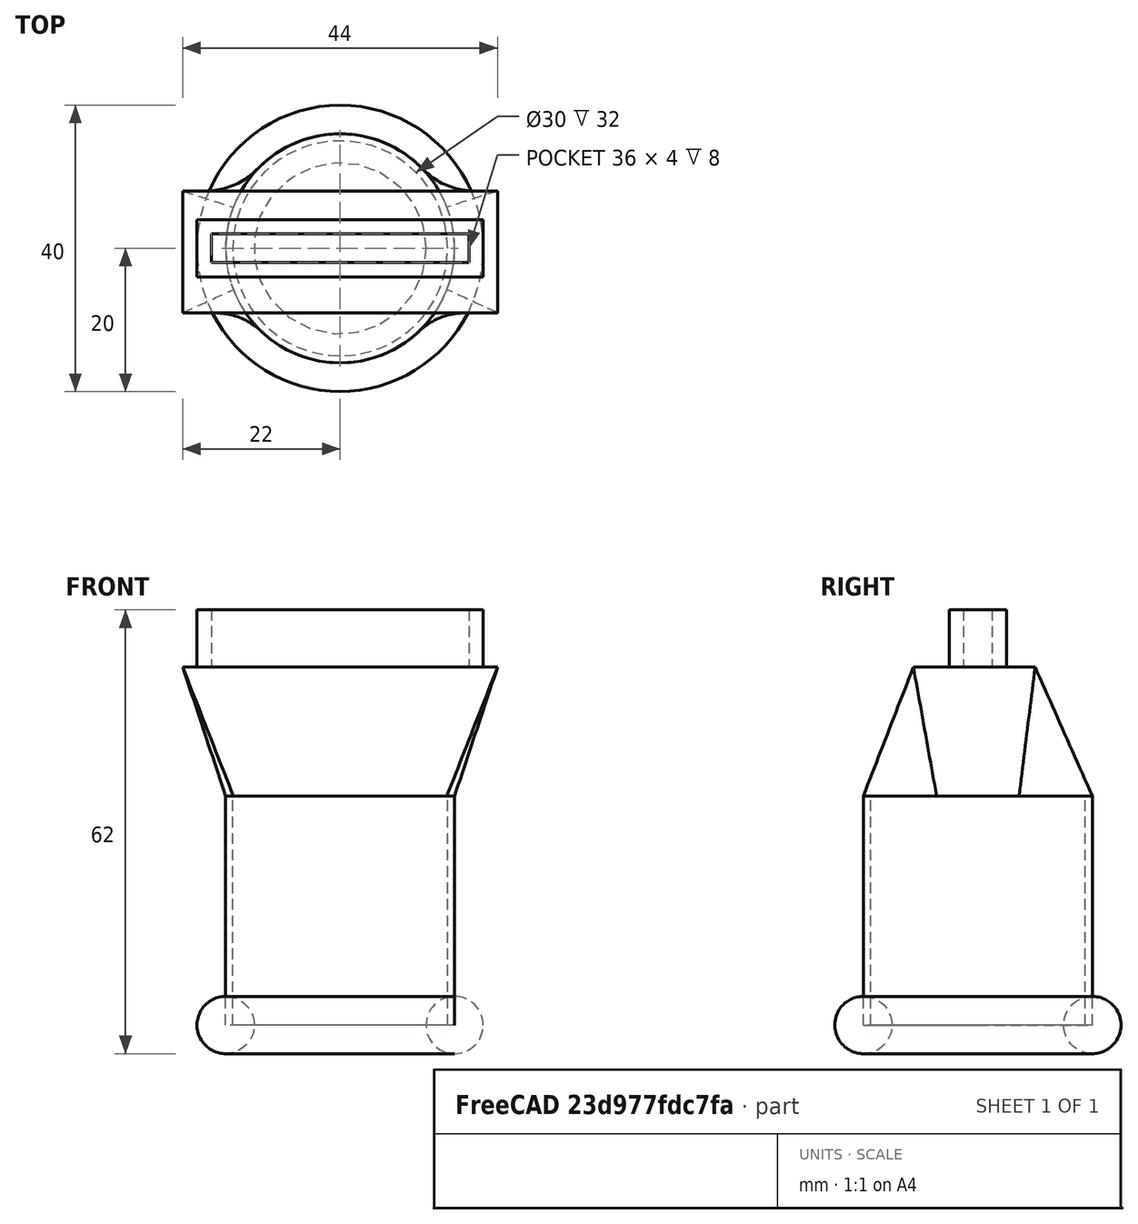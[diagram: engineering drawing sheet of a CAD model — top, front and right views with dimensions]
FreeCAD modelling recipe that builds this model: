
FCSTD DOCUMENT  (FreeCAD 0.18R16131 (Git))
Label: ADAPTER BALOON
License: All rights reserved
LicenseURL: http://en.wikipedia.org/wiki/All_rights_reserved
objects: TechDraw::DrawViewDimension×11, Sketcher::SketchObject×7, TechDraw::DrawProjGroupItem×4, PartDesign::Body×3, Part::Cylinder×2, TechDraw::DrawSVGTemplate×2, TechDraw::DrawPage×2, PartDesign::Plane×1, PartDesign::AdditiveLoft×1, PartDesign::Pad×1, Part::Torus×1, PartDesign::Pocket×1, Part::Cut×1, TechDraw::DrawViewPart×1, TechDraw::DrawProjGroup×1
note: 21 computed .brp shape members not serialized (recipe doc carries the construction recipe); baked Part::Feature solids carry a one-line shape summary decoded from their .brp

FEATURE [Sketcher::SketchObject] Sketch001
  MapMode = 5
  Placement = pos=(0,0,32) rot=(0,0,1;0rad)
  sketch-geometry (1):
    g0: Circle CenterX=0 CenterY=0 CenterZ=0 NormalX=0 NormalY=0 NormalZ=1 AngleXU=0 Radius=16
  constraints (2):
    c: Coincident(g-1,g0)
    c: Radius(g0) = 16
FEATURE [PartDesign::Plane] DatumPlane001
  AttachmentOffset = pos=(0,0,50) rot=(0,0,1;0rad)
  Length = 51.4972
  MapMode = 45
  Placement = pos=(8e-15,0,50) rot=(0,0,1;0rad)
  ResizeMode = 0
  Width = 39.4331
FEATURE [Sketcher::SketchObject] Sketch002
  MapMode = 5
  Placement = pos=(8e-15,0,50) rot=(0,0,1;0rad)
  Support = -> [DatumPlane001]
  sketch-geometry (4):
    g0: LineSegment StartX=-22 StartY=8 StartZ=0 EndX=22 EndY=8 EndZ=0
    g1: LineSegment StartX=22 StartY=8 StartZ=0 EndX=22 EndY=-9 EndZ=0
    g2: LineSegment StartX=22 StartY=-9 StartZ=0 EndX=-22 EndY=-9 EndZ=0
    g3: LineSegment StartX=-22 StartY=-9 StartZ=0 EndX=-22 EndY=8 EndZ=0
  constraints (12):
    c: Coincident(g0,g1)
    c: Coincident(g1,g2)
    c: Coincident(g2,g3)
    c: Coincident(g3,g0)
    c: Horizontal(g0)
    c: Horizontal(g2)
    c: Vertical(g1)
    c: Vertical(g3)
    c: DistanceX(g-1,g0) = 22
    c: DistanceX(g0,g-1) = 22
    c: DistanceY(g-1,g0) = 8
    c: DistanceY(g2,g-1) = 9
FEATURE [PartDesign::AdditiveLoft] AdditiveLoft
  Closed = false
  Placement = pos=(8e-15,0,50) rot=(0,0,1;0rad)
  Profile = -> Sketch002
  Ruled = true
  Sections = -> [Sketch001]
FEATURE [Sketcher::SketchObject] Sketch005
  MapMode = 5
  Placement = pos=(8e-15,0,50) rot=(0,0,1;0rad)
  sketch-geometry (4):
    g0: LineSegment StartX=-20 StartY=4 StartZ=0 EndX=20 EndY=4 EndZ=0
    g1: LineSegment StartX=20 StartY=4 StartZ=0 EndX=20 EndY=-4 EndZ=0
    g2: LineSegment StartX=20 StartY=-4 StartZ=0 EndX=-20 EndY=-4 EndZ=0
    g3: LineSegment StartX=-20 StartY=-4 StartZ=0 EndX=-20 EndY=4 EndZ=0
  constraints (12):
    c: Coincident(g0,g1)
    c: Coincident(g1,g2)
    c: Coincident(g2,g3)
    c: Coincident(g3,g0)
    c: Horizontal(g0)
    c: Horizontal(g2)
    c: Vertical(g1)
    c: Vertical(g3)
    c: DistanceX(g-1,g0) = 20
    c: DistanceX(g0,g-1) = 20
    c: DistanceY(g-1,g0) = 4
    c: DistanceY(g2,g-1) = 4
FEATURE [PartDesign::Pad] Pad
  BaseFeature = -> AdditiveLoft
  Length = 8
  Length2 = 100
  Placement = pos=(8e-15,0,50) rot=(0,0,1;0rad)
  Profile = -> Sketch005
  Type = 0
FEATURE [Sketcher::SketchObject] Sketch006
  MapMode = 5
  Placement = pos=(9e-15,0,58) rot=(0,0,1;0rad)
  sketch-geometry (4):
    g0: LineSegment StartX=-18 StartY=2 StartZ=0 EndX=18 EndY=2 EndZ=0
    g1: LineSegment StartX=18 StartY=2 StartZ=0 EndX=18 EndY=-2 EndZ=0
    g2: LineSegment StartX=18 StartY=-2 StartZ=0 EndX=-18 EndY=-2 EndZ=0
    g3: LineSegment StartX=-18 StartY=-2 StartZ=0 EndX=-18 EndY=2 EndZ=0
  constraints (12):
    c: Coincident(g0,g1)
    c: Coincident(g1,g2)
    c: Coincident(g2,g3)
    c: Coincident(g3,g0)
    c: Horizontal(g0)
    c: Horizontal(g2)
    c: Vertical(g1)
    c: Vertical(g3)
    c: DistanceX(g-1,g0) = 18
    c: DistanceX(g0,g-1) = 18
    c: DistanceY(g-1,g0) = 2
    c: DistanceY(g2,g-1) = 2
FEATURE [Part::Torus] Torus
  Angle1 = -180
  Angle2 = 180
  Angle3 = 360
  AttacherType = Attacher::AttachEngine3D
  Radius1 = 16
  Radius2 = 4
FEATURE [Sketcher::SketchObject] Sketch008
  MapMode = 5
  Placement = pos=(0,0,0) rot=(1,0,0;3.14159rad)
  sketch-geometry (1):
    g0: Circle CenterX=0 CenterY=0 CenterZ=0 NormalX=0 NormalY=0 NormalZ=1 AngleXU=0 Radius=12
  constraints (1):
    c: Radius(g0) = 12
FEATURE [Sketcher::SketchObject] Sketch011
  MapMode = 5
  Placement = pos=(0,0,32) rot=(0,0,1;0rad)
  sketch-geometry (2):
    g0: GeomPoint X=0 Y=0 Z=0
    g1: Circle CenterX=0.010551 CenterY=-0.02388 CenterZ=0 NormalX=0 NormalY=0 NormalZ=1 AngleXU=0 Radius=16
  constraints (1):
    c: Radius(g1) = 16
FEATURE [Sketcher::SketchObject] CopySketch009
  Placement = pos=(8e-15,0,50) rot=(0,0,1;0rad)
  sketch-geometry (4):
    g0: LineSegment StartX=-22 StartY=8 StartZ=0 EndX=22 EndY=8 EndZ=0
    g1: LineSegment StartX=22 StartY=8 StartZ=0 EndX=22 EndY=-9 EndZ=0
    g2: LineSegment StartX=22 StartY=-9 StartZ=0 EndX=-22 EndY=-9 EndZ=0
    g3: LineSegment StartX=-22 StartY=-9 StartZ=0 EndX=-22 EndY=8 EndZ=0
  constraints (12):
    c: Coincident(g0,g1)
    c: Coincident(g1,g2)
    c: Coincident(g2,g3)
    c: Coincident(g3,g0)
    c: Horizontal(g0)
    c: Horizontal(g2)
    c: Vertical(g1)
    c: Vertical(g3)
    c: DistanceX(g-1,g0) = 22
    c: DistanceX(g0,g-1) = 22
    c: DistanceY(g-1,g0) = 8
    c: DistanceY(g2,g-1) = 9
FEATURE [PartDesign::Body] Body001
  Group = -> [Sketch011,CopySketch009]
  Origin = -> Origin001
FEATURE [Part::Cylinder] Cylinder001
  Angle = 360
  AttacherType = Attacher::AttachEngine3D
  Height = 32
  Radius = 15
FEATURE [PartDesign::Body] Body002
  Origin = -> Origin002
FEATURE [PartDesign::Pocket] Pocket
  BaseFeature = -> Pad
  Length = 8
  Length2 = 100
  Placement = pos=(8e-15,0,50) rot=(0,0,1;0rad)
  Profile = -> Sketch006
  Type = 0
FEATURE [PartDesign::Body] Body
  Group = -> [Sketch001,DatumPlane001,Sketch002,AdditiveLoft,Sketch005,Pad,Sketch006,Pocket,Sketch008]
  Origin = -> Origin
  Tip = -> Pocket
FEATURE [Part::Cylinder] Cylinder
  Angle = 360
  AttacherType = Attacher::AttachEngine3D
  Height = 32
  Radius = 16
FEATURE [Part::Cut] Cut
  Base = -> Cylinder
  Tool = -> Cylinder001
FEATURE [TechDraw::DrawSVGTemplate] Template
  EditableTexts = Designed_by_Name=Designed by Name; Drawing_number=Drawing number; FC-Date=Date; FC-SC=Scale; FC-SH=Sheet; FC-Title=Title; Subtitle=Subtitle; Weight=Weight
  Height = 210
  Orientation = 1
  Width = 297
FEATURE [TechDraw::DrawViewPart] View
  CoarseView = false
  Direction = (0,-1,0)
  Focus = 100
  HardHidden = false
  IsoCount = 0
  IsoHidden = false
  IsoVisible = false
  LockPosition = false
  Perspective = false
  Rotation = 0
  ScaleType = 0
  SeamHidden = false
  SeamVisible = false
  SmoothHidden = false
  SmoothVisible = false
  Source = -> [Body]
  X = 148.5
  Y = 105
FEATURE [TechDraw::DrawPage] Page
  KeepUpdated = true
  ProjectionType = 0
  Template = -> Template
  Views = -> [View]
FEATURE [TechDraw::DrawSVGTemplate] Template001
  EditableTexts = Approved1=Approved 1; Approved2=Approved 2; CheckedBy=Checked By; Code=Code; CompanyAddress=1234 Main St; CompanyName=Company Name; DrawingNumber=Drawing Number; DrawingTitle1=ADAPTER BALOON; DrawingTitle2=Drawing Title 2; DrawingTitle3=Drawing Title 3; DrawnBy=Drawn By; Revision=Rev; Scale=Scale; Sheet=Sheet n of m; Weight=Weight
  Height = 279.4
  Orientation = 1
  Width = 431.8
FEATURE [TechDraw::DrawProjGroupItem] ProjItem  label="Front"
  CoarseView = false
  Direction = (0,-1,0)
  Focus = 100
  HardHidden = false
  IsoCount = 0
  IsoHidden = false
  IsoVisible = false
  LockPosition = true
  Perspective = false
  Rotation = 0
  RotationVector = (1,0,0)
  Scale = 2
  ScaleType = 2
  SeamHidden = false
  SeamVisible = false
  SmoothHidden = false
  SmoothVisible = false
  Source = -> [Body]
  Type = 0
  X = 0
  Y = 0
FEATURE [TechDraw::DrawProjGroupItem] ProjItem001  label="Left"
  CoarseView = false
  Direction = (-1,-1e-16,0)
  Focus = 100
  HardHidden = false
  IsoCount = 0
  IsoHidden = false
  IsoVisible = false
  LockPosition = false
  Perspective = false
  Rotation = 0
  RotationVector = (1e-16,-1,0)
  Scale = 2
  ScaleType = 2
  SeamHidden = false
  SeamVisible = false
  SmoothHidden = false
  SmoothVisible = false
  Source = -> [Body]
  Type = 1
  X = 103
  Y = 0
FEATURE [TechDraw::DrawProjGroupItem] ProjItem002  label="FrontTopLeft"
  CoarseView = false
  Direction = (-1,-1,1)
  Focus = 100
  HardHidden = false
  IsoCount = 0
  IsoHidden = false
  IsoVisible = false
  LockPosition = false
  Perspective = false
  Rotation = 0
  RotationVector = (1,-1,0)
  Scale = 2
  ScaleType = 2
  SeamHidden = false
  SeamVisible = false
  SmoothHidden = false
  SmoothVisible = false
  Source = -> [Body]
  Type = 6
  X = 103
  Y = -103
FEATURE [TechDraw::DrawProjGroupItem] ProjItem003  label="Top"
  CoarseView = false
  Direction = (0,0,1)
  Focus = 100
  HardHidden = false
  IsoCount = 0
  IsoHidden = false
  IsoVisible = false
  LockPosition = false
  Perspective = false
  Rotation = 0
  RotationVector = (1,0,0)
  Scale = 2
  ScaleType = 2
  SeamHidden = false
  SeamVisible = false
  SmoothHidden = false
  SmoothVisible = false
  Source = -> [Body]
  Type = 4
  X = 0
  Y = -103
FEATURE [TechDraw::DrawProjGroup] ProjGroup
  Anchor = -> ProjItem
  AutoDistribute = true
  LockPosition = false
  ProjectionType = 0
  Rotation = 0
  Scale = 2
  ScaleType = 2
  Source = -> [Body]
  Views = -> [ProjItem,ProjItem001,ProjItem002,ProjItem003]
  X = 87.6395
  Y = 212.497
  spacingX = 15
  spacingY = 15
FEATURE [TechDraw::DrawViewDimension] Dimension
  Arbitrary = false
  FormatSpec = %.2f
  LockPosition = false
  MeasureType = 1
  OverTolerance = 0
  References2D = -> [ProjItem]
  Rotation = 0
  ScaleType = 0
  Type = 1
  UnderTolerance = 0
  X = -3.81315
  Y = -56.8519
FEATURE [TechDraw::DrawViewDimension] Dimension001
  Arbitrary = false
  FormatSpec = %.2f
  LockPosition = false
  MeasureType = 1
  OverTolerance = 0
  References2D = -> [ProjItem]
  Rotation = 0
  ScaleType = 0
  Type = 1
  UnderTolerance = 0
  X = -3.11985
  Y = -44.0258
FEATURE [TechDraw::DrawViewDimension] Dimension002
  Arbitrary = false
  FormatSpec = %.2f
  LockPosition = false
  MeasureType = 1
  OverTolerance = 0
  References2D = -> [ProjItem]
  Rotation = 0
  ScaleType = 0
  Type = 1
  UnderTolerance = 0
  X = -7.6263
  Y = 46.0516
FEATURE [TechDraw::DrawViewDimension] Dimension003
  Arbitrary = false
  FormatSpec = %.2f
  LockPosition = false
  MeasureType = 1
  OverTolerance = 0
  References2D = -> [ProjItem]
  Rotation = 0
  ScaleType = 0
  Type = 1
  UnderTolerance = 0
  X = -4.8531
  Y = 36.7462
FEATURE [TechDraw::DrawViewDimension] Dimension004
  Arbitrary = false
  FormatSpec = %.2f
  LockPosition = false
  MeasureType = 1
  OverTolerance = 0
  References2D = -> [ProjItem]
  Rotation = 0
  ScaleType = 0
  Type = 0
  UnderTolerance = 0
  X = 44.5864
  Y = -15.6263
FEATURE [TechDraw::DrawViewDimension] Dimension005
  Arbitrary = false
  FormatSpec = %.2f
  LockPosition = false
  MeasureType = 1
  OverTolerance = 0
  References2D = -> [ProjItem]
  Rotation = 0
  ScaleType = 0
  Type = 0
  UnderTolerance = 0
  X = -49.4042
  Y = -11.1199
FEATURE [TechDraw::DrawViewDimension] Dimension006
  Arbitrary = false
  FormatSpec = %.2f
  LockPosition = false
  MeasureType = 1
  OverTolerance = 0
  References2D = -> [ProjItem001]
  Rotation = 0
  ScaleType = 0
  Type = 1
  UnderTolerance = 0
  X = 0.34665
  Y = -37.7861
FEATURE [TechDraw::DrawViewDimension] Dimension007
  Arbitrary = false
  FormatSpec = %.2f
  LockPosition = false
  MeasureType = 1
  OverTolerance = 0
  References2D = -> [ProjItem001]
  Rotation = 0
  ScaleType = 0
  Type = 1
  UnderTolerance = 0
  X = -3.81315
  Y = -48.1856
FEATURE [TechDraw::DrawViewDimension] Dimension008
  Arbitrary = false
  FormatSpec = %.2f
  LockPosition = false
  MeasureType = 1
  OverTolerance = 0
  References2D = -> [ProjItem001]
  Rotation = 0
  ScaleType = 0
  Type = 1
  UnderTolerance = 0
  X = -1.42655
  Y = 41.1985
FEATURE [TechDraw::DrawViewDimension] Dimension009
  Arbitrary = false
  FormatSpec = %.2f
  LockPosition = false
  MeasureType = 1
  OverTolerance = 0
  References2D = -> [ProjItem001]
  Rotation = 0
  ScaleType = 0
  Type = 1
  UnderTolerance = 0
  X = 1.03995
  Y = 33.2797
FEATURE [TechDraw::DrawViewDimension] Dimension010
  Arbitrary = false
  FormatSpec = %.2f
  LockPosition = false
  MeasureType = 1
  OverTolerance = 0
  References2D = -> [ProjItem001]
  Rotation = 0
  ScaleType = 0
  Type = 0
  UnderTolerance = 0
  X = 48.2256
  Y = -4.88015
FEATURE [TechDraw::DrawPage] Page001
  KeepUpdated = true
  ProjectionType = 0
  Template = -> Template001
  Views = -> [ProjGroup,Dimension,Dimension001,Dimension002,Dimension003,Dimension004,Dimension005,Dimension006,Dimension007,Dimension008,Dimension009,Dimension010]
